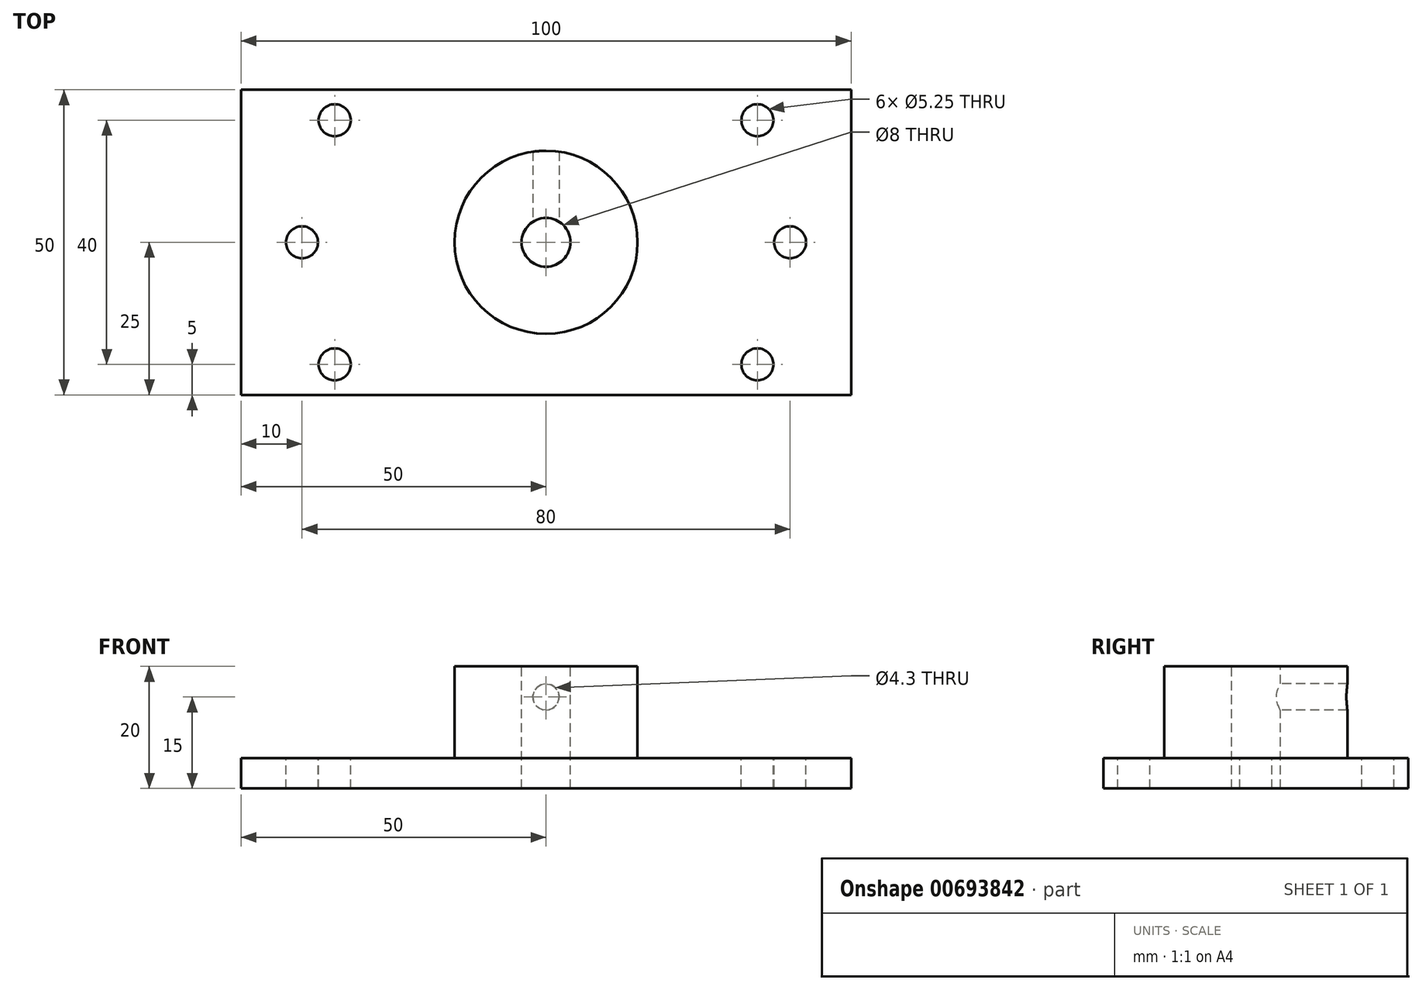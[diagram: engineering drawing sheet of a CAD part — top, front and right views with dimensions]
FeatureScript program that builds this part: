
annotation { "Feature Type Name" : "Feature", "Feature Type Description" : "" }
export const myFeature = defineFeature(function(context is Context, id is Id, definition is map)
    precondition{}
    {
        {
            var Q0;
            Q0=qCreatedBy(makeId("Top.planeOp"),FACE);
            var sketch = newSketch(context, id + "F0", { "sketchPlane" : qUnion([Q0])});
            skLineSegment(sketch, "E0.bottom", {"start": v(50, -25) * mm, "end": v(-50, -25) * mm});
            skLineSegment(sketch, "E0.top", {"start": v(50, 25) * mm, "end": v(-50, 25) * mm});
            skLineSegment(sketch, "E0.left", {"start": v(50, -25) * mm, "end": v(50, 25) * mm});
            skLineSegment(sketch, "E0.right", {"start": v(-50, -25) * mm, "end": v(-50, 25) * mm});
            skPoint(sketch, "E0.middle", {"position": v(0, 0) * mm});
            skSolve(sketch);
        }
        {
            var Q0;
            Q0=makeQuery(id+"F0.imprint","IMPRINT",FACE,{"disambiguationData":[TD([[makeQuery(id+"F0.imprint","IMPRINT",EDGE,{"derivedFrom":sQuery(id+"F0.wireOp",EDGE,"E0.bottom")}),-1.0]])]});
            extrude(context, id + "F1", {"entities" : qUnion([Q0]), "depth" : 5 * mm, "offsetDistance" : 25 * mm});
        }
        {
            var Q0;
            Q0=makeQuery(id+"F1.opExtrude","CAP_FACE",FACE,{"disambiguationData":[OSD([sQuery(id+"F0.wireOp",EDGE,"E0.bottom"),sQuery(id+"F0.wireOp",EDGE,"E0.top"),sQuery(id+"F0.wireOp",EDGE,"E0.left"),sQuery(id+"F0.wireOp",EDGE,"E0.right")])],"isStart":false});
            var sketch = newSketch(context, id + "F2", { "sketchPlane" : qUnion([Q0])});
            skCircle(sketch, "E1", {"center": v(0, 0) * mm, "radius": 15 * mm});
            skSolve(sketch);
        }
        {
            var Q0;
            Q0=makeQuery(id+"F2.imprint","IMPRINT",FACE,{"disambiguationData":[TD([[makeQuery(id+"F2.imprint","IMPRINT",EDGE,{"derivedFrom":sQuery(id+"F2.wireOp",EDGE,"E1")}),1.0]])]});
            extrude(context, id + "F3", {"entities" : qUnion([Q0]), "operationType" : NewBodyOperationType.ADD, "depth" : 15 * mm, "offsetDistance" : 25 * mm});
        }
        {
            var Q0;
            Q0=makeQuery(id+"F3.opExtrude","CAP_FACE",FACE,{"disambiguationData":[OSD([sQuery(id+"F2.wireOp",EDGE,"E1")])],"isStart":false});
            var sketch = newSketch(context, id + "F4", { "sketchPlane" : qUnion([Q0])});
            skCircle(sketch, "E2", {"center": v(0, 0) * mm, "radius": 4 * mm});
            skSolve(sketch);
        }
        {
            var Q0;
            Q0=makeQuery(id+"F4.imprint","IMPRINT",FACE,{"disambiguationData":[TD([[makeQuery(id+"F4.imprint","IMPRINT",EDGE,{"derivedFrom":sQuery(id+"F4.wireOp",EDGE,"E2")}),1.0]])]});
            extrude(context, id + "F5", {"entities" : qUnion([Q0]), "operationType" : NewBodyOperationType.REMOVE, "endBound" : BoundingType.THROUGH_ALL, "oppositeDirection" : true, "depth" : 25 * mm, "offsetDistance" : 25 * mm});
        }
        {
            var Q0;
            Q0=makeQuery(id+"F1.opExtrude","CAP_FACE",FACE,{"disambiguationData":[OSD([sQuery(id+"F0.wireOp",EDGE,"E0.bottom"),sQuery(id+"F0.wireOp",EDGE,"E0.top"),sQuery(id+"F0.wireOp",EDGE,"E0.left"),sQuery(id+"F0.wireOp",EDGE,"E0.right")])],"isStart":false});
            var sketch = newSketch(context, id + "F6", { "sketchPlane" : qUnion([Q0])});
            skCircle(sketch, "E3", {"center": v(0, 0) * mm, "radius": 40 * mm, "construction": true});
            skPoint(sketch, "E4", {"position": v(-40, 0) * mm});
            skPoint(sketch, "E5", {"position": v(-34.64, 20) * mm});
            skPoint(sketch, "E6", {"position": v(-34.64, -20) * mm});
            skLineSegment(sketch, "E7", {"start": v(0, 0) * mm, "end": v(-34.64, -20) * mm, "construction": true});
            skLineSegment(sketch, "E8", {"start": v(0, 0) * mm, "end": v(-40, 0) * mm, "construction": true});
            skLineSegment(sketch, "E9", {"start": v(0, 0) * mm, "end": v(-34.64, 20) * mm, "construction": true});
            skPoint(sketch, "E10.MirrorP", {"position": v(34.64, 20) * mm});
            skPoint(sketch, "E11.MirrorP", {"position": v(40, 0) * mm});
            skPoint(sketch, "E12.MirrorP", {"position": v(34.64, -20) * mm});
            skLineSegment(sketch, "E13.MirrorCS", {"start": v(0, 0) * mm, "end": v(34.64, 20) * mm, "construction": true});
            skLineSegment(sketch, "E14.MirrorCS", {"start": v(0, 0) * mm, "end": v(40, 0) * mm, "construction": true});
            skLineSegment(sketch, "E15.MirrorCS", {"start": v(0, 0) * mm, "end": v(34.64, -20) * mm, "construction": true});
            skSolve(sketch);
        }
        {
            var Q0;
            Q0=sQuery(id+"F6.wireOp",VERTEX,"E5");
            var Q1;
            Q1=sQuery(id+"F6.wireOp",VERTEX,"E4");
            var Q2;
            Q2=sQuery(id+"F6.wireOp",VERTEX,"E6");
            var Q3;
            Q3=sQuery(id+"F6.wireOp",VERTEX,"E10.MirrorP");
            var Q4;
            Q4=sQuery(id+"F6.wireOp",VERTEX,"E11.MirrorP");
            var Q5;
            Q5=sQuery(id+"F6.wireOp",VERTEX,"E12.MirrorP");
            var Q6;
            Q6=makeQuery(id+"F1.opExtrude","SWEPT_BODY",BODY,{"disambiguationData":[OSD([sQuery(id+"F0.wireOp",EDGE,"E0.bottom"),sQuery(id+"F0.wireOp",EDGE,"E0.top"),sQuery(id+"F0.wireOp",EDGE,"E0.left"),sQuery(id+"F0.wireOp",EDGE,"E0.right")])]});
            hole(context, id + "F7", {"style" : HoleStyle.SIMPLE, "endStyle" : HoleEndStyle.THROUGH, "standardTappedOrClearance" : lookupTablePath({ "standard" : "ISO", "fit" : "Close", "size" : "M5", "type" : "Clearance" }), "standardBlindInLast" : lookupTablePath({ "fit" : "Close", "standard" : "ISO", "size" : "M5", "type" : "Clearance" }), "holeDiameter" : 5.25 * mm, "majorDiameter" : 5 * mm, "isTappedThrough" : true, "tappedDepth" : 17.6 * mm, "tapClearance" : 3, "locations" : qUnion([Q0, Q1, Q2, Q3, Q4, Q5]), "scope" : qUnion([Q6])});
        }
        {
            var Q0;
            Q0=qCreatedBy(makeId("Front.planeOp"),FACE);
            var sketch = newSketch(context, id + "F8", { "sketchPlane" : qUnion([Q0])});
            skCircle(sketch, "E16", {"center": v(0, 15) * mm, "radius": 2.15 * mm});
            skSolve(sketch);
        }
        {
            var Q0;
            Q0=makeQuery(id+"F8.imprint","IMPRINT",FACE,{"disambiguationData":[TD([[makeQuery(id+"F8.imprint","IMPRINT",EDGE,{"derivedFrom":sQuery(id+"F8.wireOp",EDGE,"E16")}),1.0]])]});
            extrude(context, id + "F9", {"entities" : qUnion([Q0]), "operationType" : NewBodyOperationType.REMOVE, "endBound" : BoundingType.THROUGH_ALL, "oppositeDirection" : true, "depth" : 25 * mm, "offsetDistance" : 25 * mm});
        }
    });
